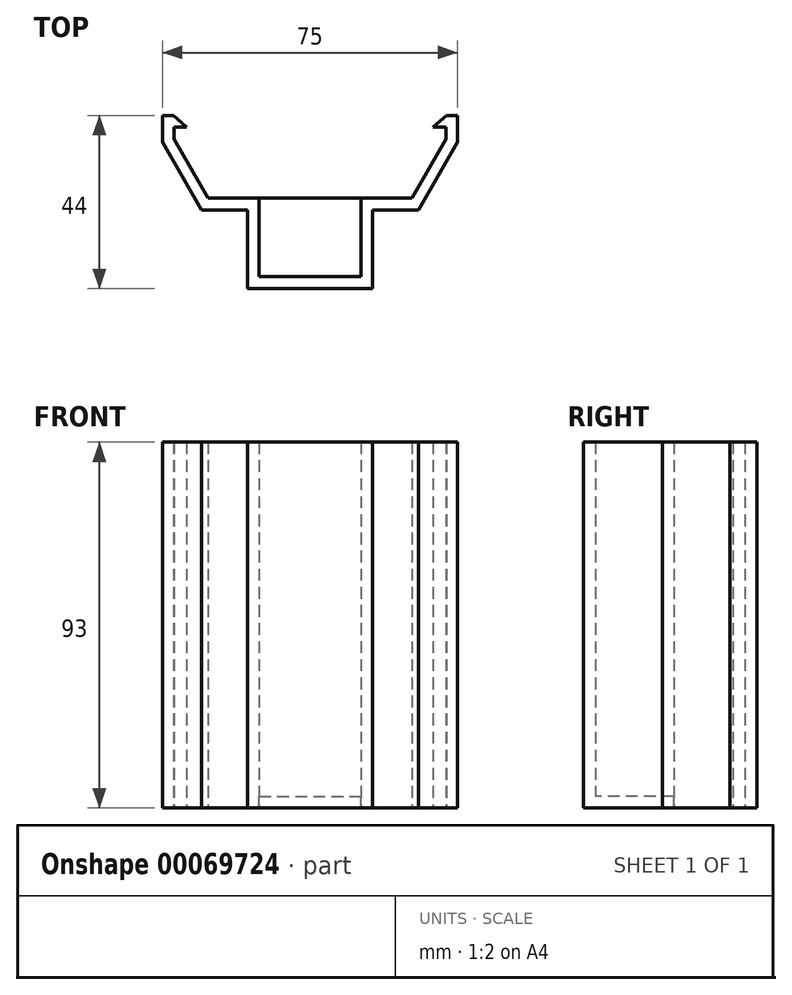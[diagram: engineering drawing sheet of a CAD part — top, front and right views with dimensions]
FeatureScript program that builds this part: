
annotation { "Feature Type Name" : "Feature", "Feature Type Description" : "" }
export const myFeature = defineFeature(function(context is Context, id is Id, definition is map)
    precondition{}
    {
        {
            var Q0;
            Q0=qCreatedBy(makeId("Top.planeOp"),FACE);
            var sketch = newSketch(context, id + "F0", { "sketchPlane" : qUnion([Q0])});
            skLineSegment(sketch, "E0", {"start": v(27.58, 0) * mm, "end": v(37.5, 17.2) * mm});
            skLineSegment(sketch, "E1", {"start": v(37.5, 17.2) * mm, "end": v(37.5, 24) * mm});
            skLineSegment(sketch, "E2", {"start": v(25.85, 3) * mm, "end": v(34.5, 18) * mm});
            skLineSegment(sketch, "E3", {"start": v(34.5, 18) * mm, "end": v(34.5, 21) * mm});
            skLineSegment(sketch, "E4", {"start": v(37.5, 24) * mm, "end": v(34.64, 24) * mm});
            skLineSegment(sketch, "E5", {"start": v(34.5, 21) * mm, "end": v(31.3, 21) * mm});
            skLineSegment(sketch, "E6", {"start": v(31.3, 21) * mm, "end": v(34.64, 24) * mm});
            skLineSegment(sketch, "E7.0.MirrorCS", {"start": v(-34.5, 21) * mm, "end": v(-31.3, 21) * mm});
            skLineSegment(sketch, "E7.1.MirrorCS", {"start": v(-31.3, 21) * mm, "end": v(-34.64, 24) * mm});
            skLineSegment(sketch, "E7.2.MirrorCS", {"start": v(-37.5, 24) * mm, "end": v(-34.64, 24) * mm});
            skLineSegment(sketch, "E7.4.MirrorCS", {"start": v(-25.85, 3) * mm, "end": v(-34.5, 18) * mm});
            skLineSegment(sketch, "E7.6.MirrorCS", {"start": v(-37.5, 17.2) * mm, "end": v(-37.5, 24) * mm});
            skLineSegment(sketch, "E7.7.MirrorCS", {"start": v(-34.5, 18) * mm, "end": v(-34.5, 21) * mm});
            skLineSegment(sketch, "E7.8.MirrorCS", {"start": v(-27.58, 0) * mm, "end": v(-37.5, 17.2) * mm});
            skLineSegment(sketch, "E8", {"start": v(-25.85, 3) * mm, "end": v(-12.92, 3) * mm});
            skLineSegment(sketch, "E9", {"start": v(25.85, 3) * mm, "end": v(12.92, 3) * mm});
            skLineSegment(sketch, "E10", {"start": v(-12.92, 3) * mm, "end": v(-12.92, -17) * mm});
            skLineSegment(sketch, "E11", {"start": v(12.92, 3) * mm, "end": v(12.92, -17) * mm});
            skLineSegment(sketch, "E12", {"start": v(-12.92, -17) * mm, "end": v(12.92, -17) * mm});
            skLineSegment(sketch, "E13", {"start": v(-12.92, -20) * mm, "end": v(12.92, -20) * mm});
            skLineSegment(sketch, "E14", {"start": v(12.92, 0) * mm, "end": v(15.92, 0) * mm, "construction": true});
            skLineSegment(sketch, "E15", {"start": v(-12.92, 0) * mm, "end": v(-15.92, 0) * mm, "construction": true});
            skLineSegment(sketch, "E16", {"start": v(-12.92, -20) * mm, "end": v(-15.92, -20) * mm});
            skLineSegment(sketch, "E17", {"start": v(12.92, -20) * mm, "end": v(15.92, -20) * mm});
            skLineSegment(sketch, "E18", {"start": v(-27.58, 0) * mm, "end": v(-15.92, 0) * mm});
            skLineSegment(sketch, "E19", {"start": v(-15.92, -20) * mm, "end": v(-15.92, 0) * mm});
            skLineSegment(sketch, "E20", {"start": v(27.58, 0) * mm, "end": v(15.92, 0) * mm});
            skLineSegment(sketch, "E21", {"start": v(15.92, -20) * mm, "end": v(15.92, 0) * mm});
            skSolve(sketch);
        }
        {
            var Q0;
            Q0=makeQuery(id+"F0.imprint","IMPRINT",FACE,{"disambiguationData":[TD([[makeQuery(id+"F0.imprint","IMPRINT",EDGE,{"derivedFrom":sQuery(id+"F0.wireOp",EDGE,"E0")}),1.0]])]});
            extrude(context, id + "F1", {"entities" : qUnion([Q0]), "depth" : 93 * mm});
        }
        {
            var Q0;
            Q0=qCreatedBy(makeId("Top.planeOp"),FACE);
            var sketch = newSketch(context, id + "F2", { "sketchPlane" : qUnion([Q0])});
            skLineSegment(sketch, "E22", {"start": v(-15.58, 2.93) * mm, "end": v(15.19, 2.93) * mm});
            skLineSegment(sketch, "E23", {"start": v(15.19, 2.93) * mm, "end": v(15.19, -18.85) * mm});
            skLineSegment(sketch, "E24", {"start": v(15.19, -18.85) * mm, "end": v(-15.58, -18.85) * mm});
            skLineSegment(sketch, "E25", {"start": v(-15.58, -18.85) * mm, "end": v(-15.58, 2.93) * mm});
            skSolve(sketch);
        }
        {
            var Q0;
            Q0=makeQuery(id+"F2.imprint","IMPRINT",FACE,{"disambiguationData":[TD([[makeQuery(id+"F2.imprint","IMPRINT",EDGE,{"derivedFrom":sQuery(id+"F2.wireOp",EDGE,"E22")}),-1.0]])]});
            extrude(context, id + "F3", {"entities" : qUnion([Q0]), "operationType" : NewBodyOperationType.ADD, "depth" : 3 * mm});
        }
    });
